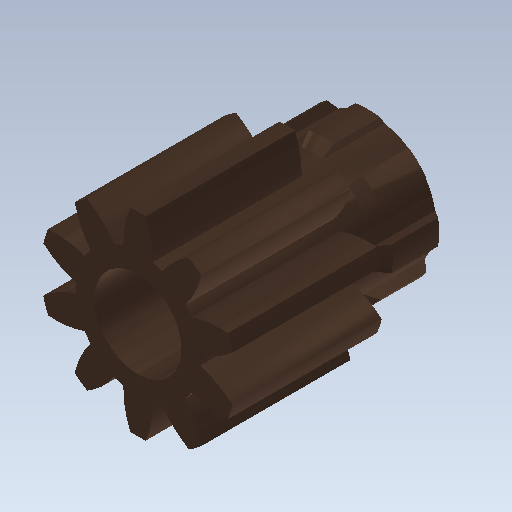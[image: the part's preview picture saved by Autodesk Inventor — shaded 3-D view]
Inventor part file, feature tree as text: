
AUTODESK INVENTOR PART (.ipt)
format: ipt  version: 2020 (Build 240168000, 168)  size: 280,064 bytes
history: native  units: mm (DEFAULTED — no unit token found)
features: sketch x5, extrude x4, plane x3, other x3, chamfer x2, pattern_circular x1, projected_geometry x1
ambient origin geometry x8: Origin, YZ Plane, XZ Plane, XY Plane, X Axis, Y Axis, Z Axis, Center Point
bodies: Solid1 (feature_tree)
feature tree (19):
  extrude  "Extrusion1"  Depth=2.4mm TaperAngle=0.0deg
  plane  "Work Plane2"
  plane  "Work Plane8"
  plane  "Work Plane9"
  other  "Цилиндрическое зубчатое зацепление"
  extrude  "Выдавливание2"  Depth=10.0mm TaperAngle=0.0deg
  extrude  "Выдавливание3"  Depth=1.4mm
  chamfer  "Фаска1"  Distance=3.141593mm
  chamfer  "Фаска2"  [1 undecoded]
  pattern_circular  "Круговой массив1"  [2 undecoded]
  extrude  "Выдавливание4"  Depth=1.4mm
  sketch  "Sketch1"  dims[d0=3.135mm d1=2.4mm d2=0.0mm]
  sketch  "Sketch2"  dims[d3=2.5mm d4=10.0mm d5=0.0mm d16=6.0mm d17=0.0mm d34=3.141593mm d39=0.0mm d41=0.0mm d43=6.0mm d46=6.0mm d47=0.0mm d48=0.0mm d49=2.0mm d50=1.4mm d51=0.0mm d52=0.15mm d53=3.490659mm d54=1.0mm d55=0.0mm d56=0.15mm d57=2.0mm d58=45.0deg d59=0.15mm d60=0.1mm d61=45.0deg d62=80.0mm d63=360.0deg d65=1.4mm d66=8.0mm d67=0.0mm]
  other  "Srf1"
  sketch  "Эскиз3"
  sketch  "Эскиз4"
  projected_geometry  "Спроецированная петля1"
  sketch  "Эскиз5"
  other  "Средний диаметр"
note: 3 required parameter values undecoded (feature->parameter linkage not recoverable at this tier; creation-order binding heuristic only, values carry confidence <= 0.55)
